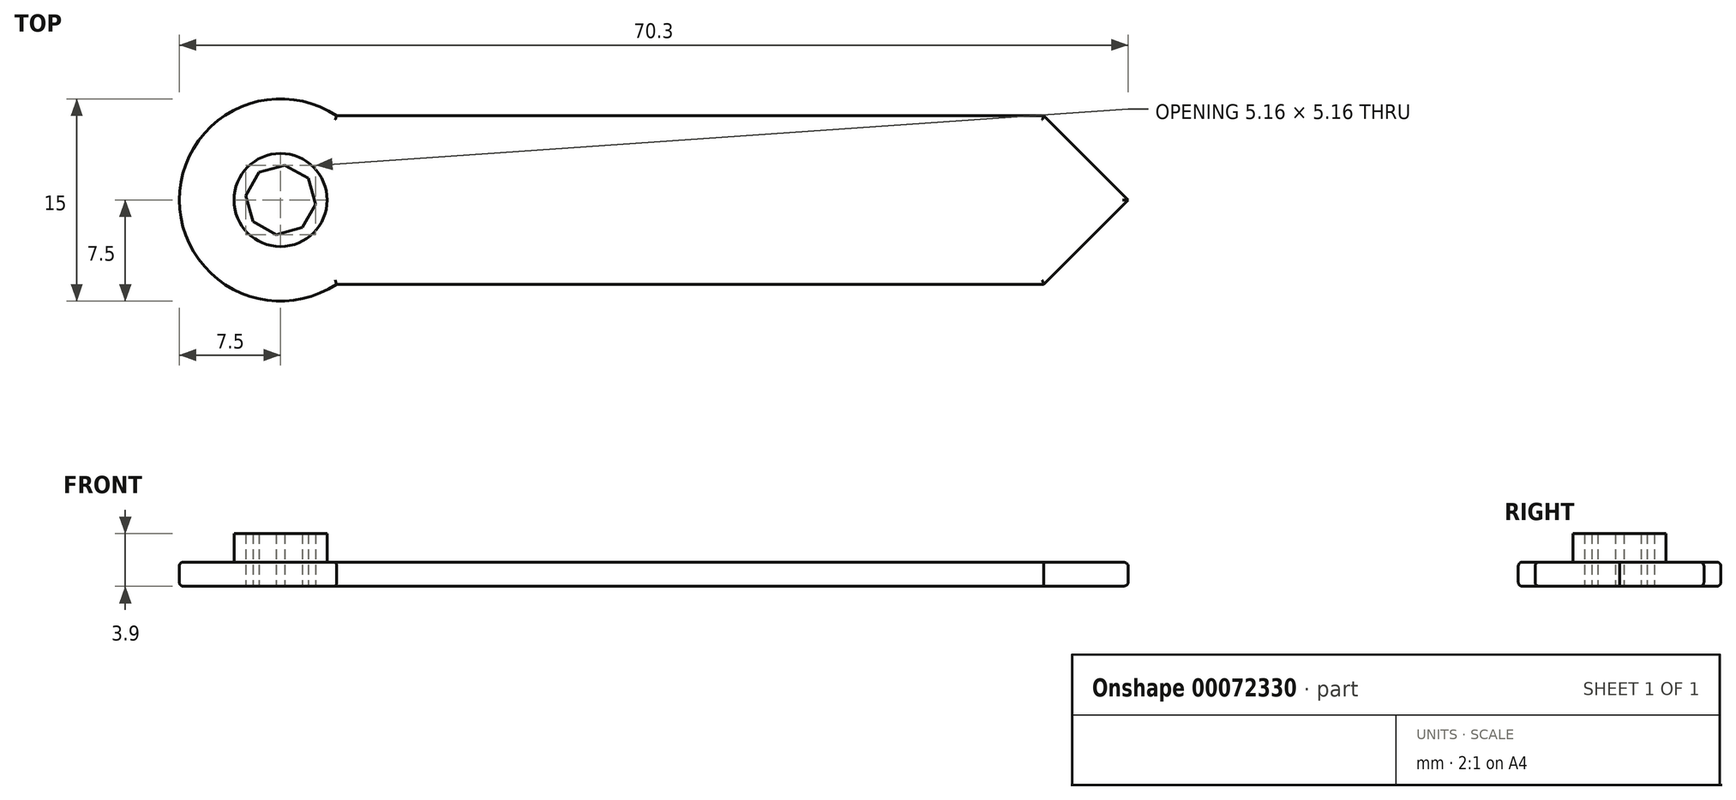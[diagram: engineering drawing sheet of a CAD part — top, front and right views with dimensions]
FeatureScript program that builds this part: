
annotation { "Feature Type Name" : "Feature", "Feature Type Description" : "" }
export const myFeature = defineFeature(function(context is Context, id is Id, definition is map)
    precondition{}
    {
        {
            var Q0;
            Q0=qCreatedBy(makeId("Top.planeOp"),FACE);
            var sketch = newSketch(context, id + "F0", { "sketchPlane" : qUnion([Q0])});
            skArc(sketch, "E0", {"start": v(4.15, 6.25) * mm, "mid": v(-7.5, 0) * mm, "end": v(4.15, -6.25) * mm});
            skCircle(sketch, "E1.cCircle", {"center": v(0, 0) * mm, "radius": 2.6 * mm, "construction": true});
            skLineSegment(sketch, "E1.0", {"start": v(1.6, -2.05) * mm, "end": v(-0.32, -2.58) * mm});
            skLineSegment(sketch, "E1.1", {"start": v(-0.32, -2.58) * mm, "end": v(-2.05, -1.6) * mm});
            skLineSegment(sketch, "E1.2", {"start": v(-2.05, -1.6) * mm, "end": v(-2.58, 0.32) * mm});
            skLineSegment(sketch, "E1.3", {"start": v(-2.58, 0.32) * mm, "end": v(-1.6, 2.05) * mm});
            skLineSegment(sketch, "E1.4", {"start": v(-1.6, 2.05) * mm, "end": v(0.32, 2.58) * mm});
            skLineSegment(sketch, "E1.5", {"start": v(0.32, 2.58) * mm, "end": v(2.05, 1.6) * mm});
            skLineSegment(sketch, "E1.6", {"start": v(2.05, 1.6) * mm, "end": v(2.58, -0.32) * mm});
            skLineSegment(sketch, "E1.7", {"start": v(2.58, -0.32) * mm, "end": v(1.6, -2.05) * mm});
            skLineSegment(sketch, "E2", {"start": v(4.15, 6.25) * mm, "end": v(56.55, 6.25) * mm});
            skLineSegment(sketch, "E3", {"start": v(56.55, 6.25) * mm, "end": v(62.8, 0) * mm});
            skLineSegment(sketch, "E4.MirrorCS", {"start": v(4.15, -6.25) * mm, "end": v(56.55, -6.25) * mm});
            skLineSegment(sketch, "E5.MirrorCS", {"start": v(56.55, -6.25) * mm, "end": v(62.8, 0) * mm});
            skCircle(sketch, "E6", {"center": v(0, 0) * mm, "radius": 3.45 * mm});
            skSolve(sketch);
        }
        {
            var Q0;
            Q0=makeQuery(id+"F0.imprint","IMPRINT",FACE,{"disambiguationData":[TD([[makeQuery(id+"F0.imprint","IMPRINT",EDGE,{"derivedFrom":sQuery(id+"F0.wireOp",EDGE,"E0")}),1.0]])]});
            extrude(context, id + "F1", {"entities" : qUnion([Q0]), "depth" : 1.8 * mm});
        }
        {
            var Q0;
            Q0=makeQuery(id+"F0.imprint","IMPRINT",FACE,{"disambiguationData":[TD([[makeQuery(id+"F0.imprint","IMPRINT",EDGE,{"derivedFrom":sQuery(id+"F0.wireOp",EDGE,"E1.0")}),1.0]])]});
            extrude(context, id + "F2", {"entities" : qUnion([Q0]), "operationType" : NewBodyOperationType.ADD, "depth" : 3.9 * mm});
        }
        {
            var Q0;
            Q0=makeQuery(id+"F1.opExtrude","CAP_EDGE",EDGE,{"disambiguationData":[OSD([sQuery(id+"F0.wireOp",EDGE,"E0")])],"isStart":false});
            var Q1;
            Q1=makeQuery(id+"F1.opExtrude","CAP_EDGE",EDGE,{"disambiguationData":[OSD([sQuery(id+"F0.wireOp",EDGE,"E2")])],"isStart":false});
            var Q2;
            Q2=makeQuery(id+"F1.opExtrude","CAP_EDGE",EDGE,{"disambiguationData":[OSD([sQuery(id+"F0.wireOp",EDGE,"E4.MirrorCS")])],"isStart":false});
            var Q3;
            Q3=makeQuery(id+"F1.opExtrude","CAP_EDGE",EDGE,{"disambiguationData":[OSD([sQuery(id+"F0.wireOp",EDGE,"E5.MirrorCS")])],"isStart":false});
            var Q4;
            Q4=makeQuery(id+"F1.opExtrude","CAP_EDGE",EDGE,{"disambiguationData":[OSD([sQuery(id+"F0.wireOp",EDGE,"E3")])],"isStart":false});
            var Q5;
            Q5=makeQuery(id+"F1.opExtrude","CAP_EDGE",EDGE,{"disambiguationData":[OSD([sQuery(id+"F0.wireOp",EDGE,"E0")])],"isStart":true});
            var Q6;
            Q6=makeQuery(id+"F1.opExtrude","CAP_EDGE",EDGE,{"disambiguationData":[OSD([sQuery(id+"F0.wireOp",EDGE,"E4.MirrorCS")])],"isStart":true});
            var Q7;
            Q7=makeQuery(id+"F1.opExtrude","CAP_EDGE",EDGE,{"disambiguationData":[OSD([sQuery(id+"F0.wireOp",EDGE,"E3")])],"isStart":true});
            var Q8;
            Q8=makeQuery(id+"F1.opExtrude","CAP_EDGE",EDGE,{"disambiguationData":[OSD([sQuery(id+"F0.wireOp",EDGE,"E5.MirrorCS")])],"isStart":true});
            var Q9;
            Q9=makeQuery(id+"F1.opExtrude","CAP_EDGE",EDGE,{"disambiguationData":[OSD([sQuery(id+"F0.wireOp",EDGE,"E2")])],"isStart":true});
            fillet(context, id + "F3", {"entities" : qUnion([Q0, Q1, Q2, Q3, Q4, Q5, Q6, Q7, Q8, Q9]), "radius" : .3 * mm, "tangentPropagation" : true, "allowEdgeOverflow" : false});
        }
    });
